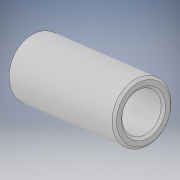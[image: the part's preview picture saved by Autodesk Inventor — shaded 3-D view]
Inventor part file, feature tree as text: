
AUTODESK INVENTOR PART (.ipt)
format: ipt  version: 2018 (Build 220112000, 112)  size: 109,056 bytes
history: native  units: mm
features: extrude x1, chamfer x1, sketch x1
ambient origin geometry x8: Origin, YZ Plane, XZ Plane, XY Plane, X Axis, Y Axis, Z Axis, Center Point
bodies: Solid1 (feature_tree)
feature tree (3):
  extrude  "Extrusion1"  Depth=2.0mm
  chamfer  "Chamfer1"  Distance=13.0mm
  sketch  "Sketch1"  dims[d0=6.0mm d1=4.0mm d2=13.0mm d3=0.0mm d4=0.25mm d5=2.0mm d6=45.0deg]
